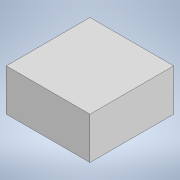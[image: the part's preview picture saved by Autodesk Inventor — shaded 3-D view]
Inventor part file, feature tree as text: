
AUTODESK INVENTOR PART (.ipt)
format: ipt  version: 2022 (Build 260153000, 153)  size: 115,200 bytes
history: native  units: mm
features: extrude x5, sketch x5
ambient origin geometry x8: Origin, YZ Plane, XZ Plane, XY Plane, X Axis, Y Axis, Z Axis, Center Point
bodies: Solid1 (feature_tree)
feature tree (10):
  extrude  "Extrusion1"  Depth=30.0mm
  extrude  "Extrusion2"  Depth=5.0mm TaperAngle=0.0deg
  extrude  "Extrusion3"  Depth=10.0mm TaperAngle=0.0deg
  extrude  "Extrusion4"  [1 undecoded]
  extrude  "Extrusion5"  [1 undecoded]
  sketch  "Sketch1"  dims[d0=30.0mm d1=30.0mm]
  sketch  "Sketch2"  dims[d2=15.0mm d3=0.0mm d4=5.0mm d5=0.0mm]
  sketch  "Sketch3"  dims[d6=10.0mm d7=0.0mm d8=10.0mm d9=0.0mm]
  sketch  "Sketch4"  dims[d10=20.0mm d11=0.0mm]
  sketch  "Sketch5"
note: 2 required parameter values undecoded (feature->parameter linkage not recoverable at this tier; creation-order binding heuristic only, values carry confidence <= 0.55)
